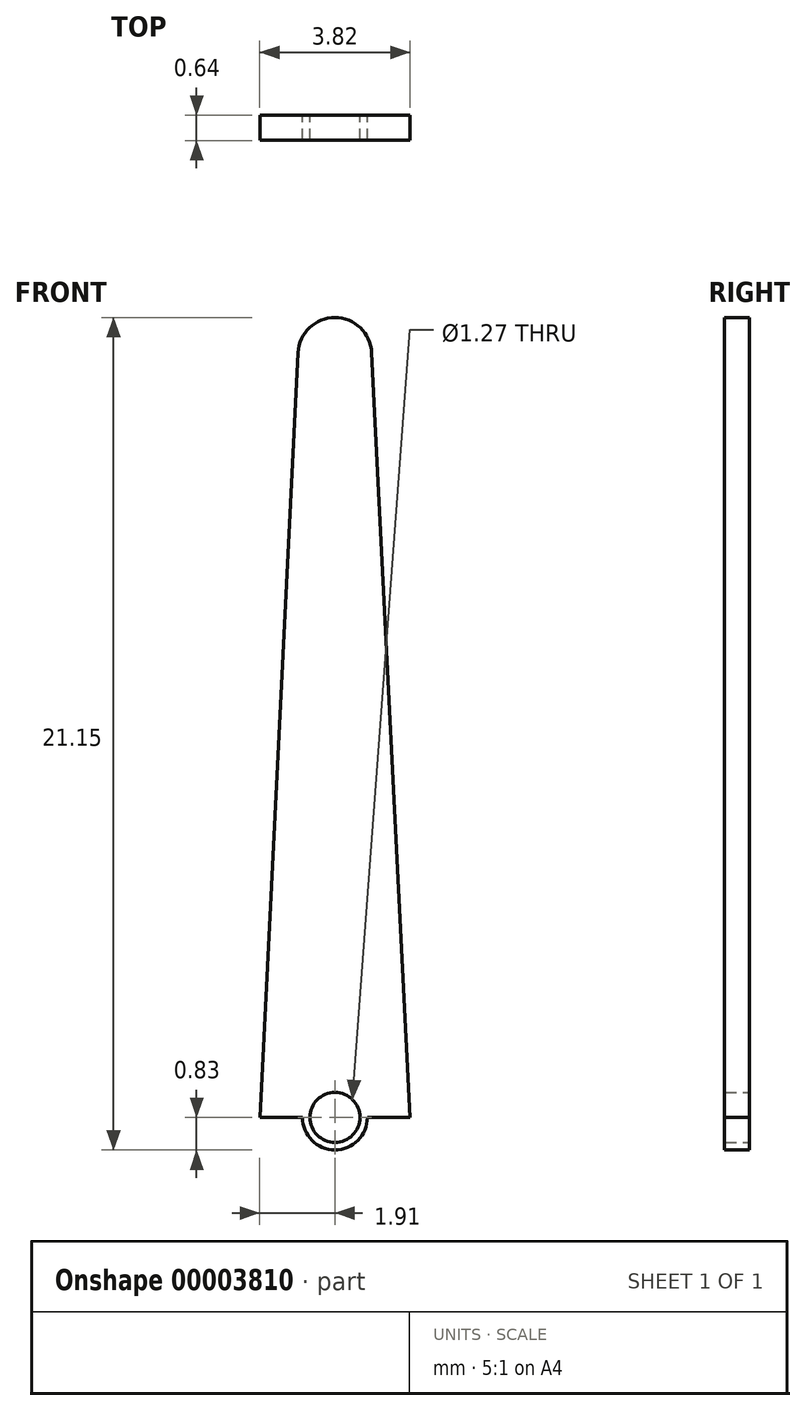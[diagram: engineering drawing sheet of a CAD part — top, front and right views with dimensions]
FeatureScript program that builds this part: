
annotation { "Feature Type Name" : "Feature", "Feature Type Description" : "" }
export const myFeature = defineFeature(function(context is Context, id is Id, definition is map)
    precondition{}
    {
        {
            var Q0;
            Q0=qCreatedBy(makeId("Front.planeOp"),FACE);
            var sketch = newSketch(context, id + "F0", { "sketchPlane" : qUnion([Q0])});
            skLineSegment(sketch, "E0.bottom", {"start": v(-1.9, 0) * mm, "end": v(1.9, 0) * mm});
            skCircle(sketch, "E1", {"center": v(0, 0) * mm, "radius": 0.83 * mm});
            skPoint(sketch, "E2.start.orphan", {"position": v(0, 20.32) * mm});
            skLineSegment(sketch, "E3", {"start": v(0, 0) * mm, "end": v(0, 20.32) * mm, "construction": true});
            skLineSegment(sketch, "E4", {"start": v(-1.9, 0) * mm, "end": v(-0.93, 19.43) * mm});
            skLineSegment(sketch, "E5", {"start": v(0, 20.32) * mm, "end": v(0, 20.32) * mm});
            skPoint(sketch, "E6.visualSharp", {"position": v(-0.89, 20.32) * mm});
            skArc(sketch, "E6.filletArc", {"start": v(0, 20.32) * mm, "mid": v(-0.64, 20.06) * mm, "end": v(-0.93, 19.43) * mm});
            skLineSegment(sketch, "E7.0.MirrorCS", {"start": v(1.9, 0) * mm, "end": v(0.93, 19.43) * mm});
            skArc(sketch, "E8.0.MirrorCS", {"start": v(0, 20.32) * mm, "mid": v(0.64, 20.06) * mm, "end": v(0.93, 19.43) * mm});
            skSolve(sketch);
        }
        {
            var Q0;
            Q0 = qSketchRegion(id + "F0", true);
            extrude(context, id + "F1", {"entities" : qUnion([Q0]), "depth" : 0.64 * mm});
        }
        {
            var Q0;
            {var subQ0=sQuery(id+"F0.wireOp",EDGE,"E1");var subQ1=sQuery(id+"F0.wireOp",EDGE,"E0.bottom");var subQ3=makeQuery(id+"F0.imprint","INTERSECT",VERTEX,{"disambiguationData":[OD(0.0)],"derivedFrom":[subQ1,subQ0]});Q0=makeQuery(id+"F0.imprint","IMPRINT",FACE,{"disambiguationData":[TD([[makeQuery(id+"F0.imprint","IMPRINT",EDGE,{"disambiguationData":[TD([[subQ3,-1.0]])],"derivedFrom":subQ1}),1.0]])]});}
            var sketch = newSketch(context, id + "F2", { "sketchPlane" : qUnion([Q0])});
            skCircle(sketch, "E9", {"center": v(0, 0) * mm, "radius": 0.64 * mm});
            skSolve(sketch);
        }
        {
            var Q0;
            {var subQ0=sQuery(id+"F0.wireOp",EDGE,"E0.bottom");var subQ1=sQuery(id+"F0.wireOp",EDGE,"E1");var subQ2=makeQuery(id+"F0.imprint","IMPRINT",EDGE,{"disambiguationData":[TD([[makeQuery(id+"F0.imprint","INTERSECT",VERTEX,{"disambiguationData":[OD(0.0)],"derivedFrom":[subQ0,subQ1]}),-1.0]])],"derivedFrom":subQ0});var subQ3=sQuery(id+"F2.wireOp",EDGE,"E9");var subQ5=makeQuery(id+"F2.imprint","INTERSECT",VERTEX,{"disambiguationData":[OD(0.0)],"derivedFrom":[subQ2,subQ3]});Q0=makeQuery(id+"F2.imprint","IMPRINT",FACE,{"disambiguationData":[TD([[makeQuery(id+"F2.imprint","IMPRINT",EDGE,{"disambiguationData":[TD([[subQ5,1.0]])],"derivedFrom":subQ3}),1.0]])]});}
            var Q1;
            {var subQ0=sQuery(id+"F0.wireOp",EDGE,"E0.bottom");var subQ1=sQuery(id+"F0.wireOp",EDGE,"E1");var subQ2=makeQuery(id+"F0.imprint","IMPRINT",EDGE,{"disambiguationData":[TD([[makeQuery(id+"F0.imprint","INTERSECT",VERTEX,{"disambiguationData":[OD(0.0)],"derivedFrom":[subQ0,subQ1]}),-1.0]])],"derivedFrom":subQ0});var subQ3=sQuery(id+"F2.wireOp",EDGE,"E9");var subQ5=makeQuery(id+"F2.imprint","INTERSECT",VERTEX,{"disambiguationData":[OD(0.0)],"derivedFrom":[subQ2,subQ3]});Q1=makeQuery(id+"F2.imprint","IMPRINT",FACE,{"disambiguationData":[TD([[makeQuery(id+"F2.imprint","IMPRINT",EDGE,{"disambiguationData":[TD([[subQ5,-1.0]])],"derivedFrom":subQ3}),1.0]])]});}
            extrude(context, id + "F3", {"entities" : qUnion([Q0, Q1]), "operationType" : NewBodyOperationType.REMOVE, "depth" : 25.4 * mm});
        }
    });
